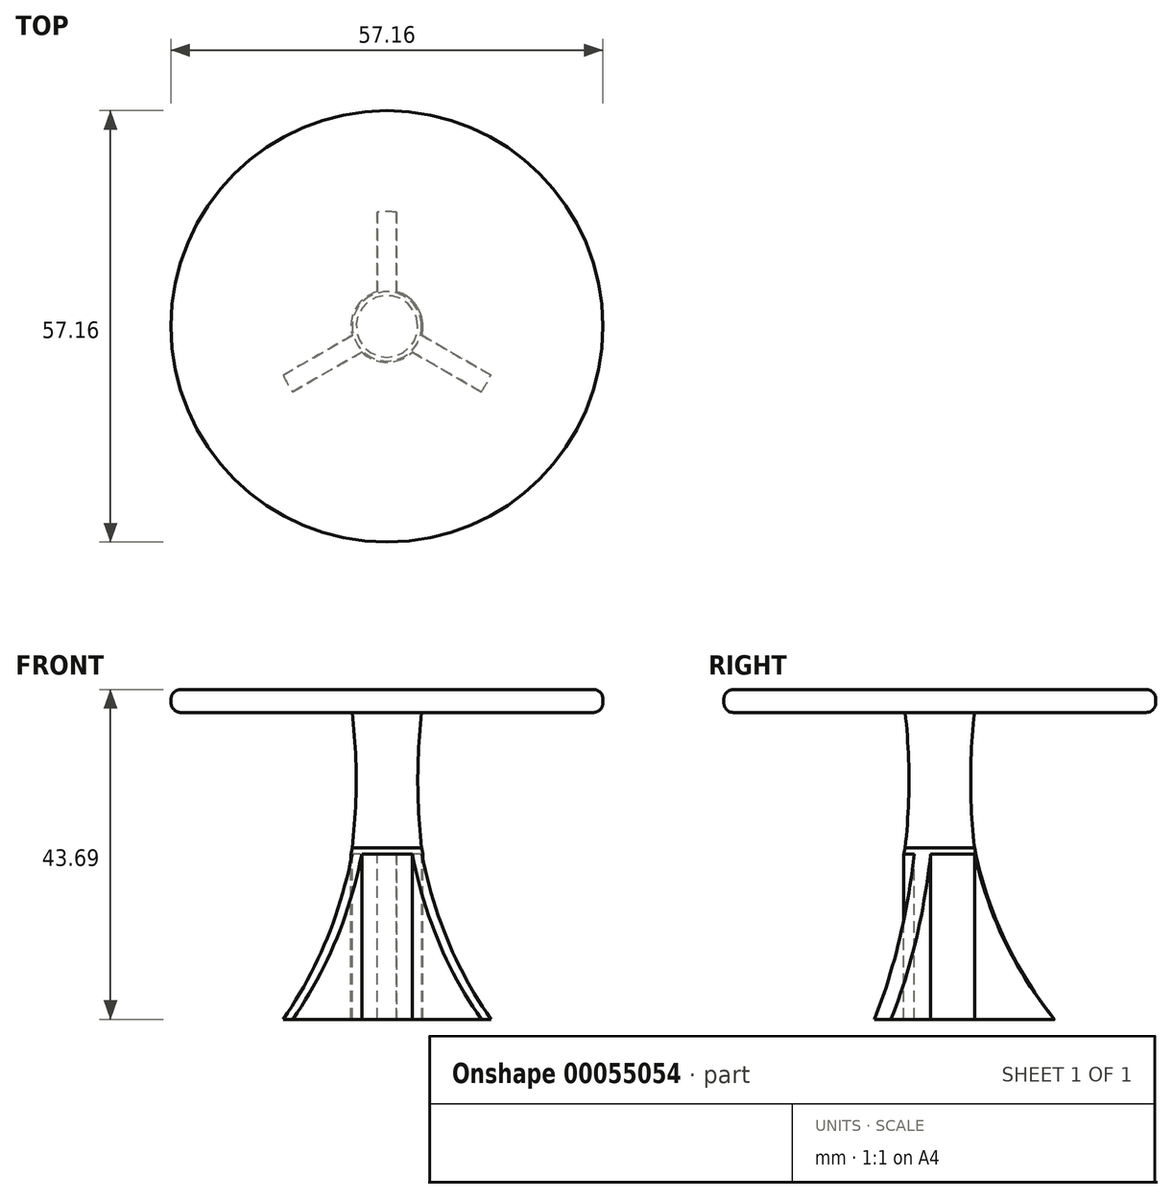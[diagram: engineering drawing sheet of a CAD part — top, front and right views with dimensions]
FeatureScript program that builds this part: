
annotation { "Feature Type Name" : "Feature", "Feature Type Description" : "" }
export const myFeature = defineFeature(function(context is Context, id is Id, definition is map)
    precondition{}
    {
        {
            var Q0;
            Q0=qCreatedBy(makeId("Top.planeOp"),FACE);
            var sketch = newSketch(context, id + "F0", { "sketchPlane" : qUnion([Q0])});
            skCircle(sketch, "E0", {"center": v(0, 0) * mm, "radius": 15.24 * mm});
            skSolve(sketch);
        }
        {
            var Q0;
            Q0 = qSketchRegion(id + "F0", true);
            extrude(context, id + "F1", {"entities" : qUnion([Q0]), "oppositeDirection" : true, "depth" : 40.64 * mm});
        }
        {
            var Q0;
            Q0=qCreatedBy(makeId("Top.planeOp"),FACE);
            var sketch = newSketch(context, id + "F2", { "sketchPlane" : qUnion([Q0])});
            skArc(sketch, "E1", {"start": v(-3.34, -3.4) * mm, "mid": v(0, -4.76) * mm, "end": v(3.34, -3.4) * mm});
            skLineSegment(sketch, "E2", {"start": v(0, 4.76) * mm, "end": v(0, 15.24) * mm, "construction": true});
            skLineSegment(sketch, "E3", {"start": v(-4.12, -2.38) * mm, "end": v(-13.2, -7.62) * mm, "construction": true});
            skLineSegment(sketch, "E4", {"start": v(4.12, -2.38) * mm, "end": v(13.2, -7.62) * mm, "construction": true});
            skLineSegment(sketch, "E5", {"start": v(0, 4.76) * mm, "end": v(-4.12, -2.38) * mm, "construction": true});
            skLineSegment(sketch, "E6", {"start": v(4.12, -2.38) * mm, "end": v(0, 4.76) * mm, "construction": true});
            skLineSegment(sketch, "E7", {"start": v(-4.12, -2.38) * mm, "end": v(4.12, -2.38) * mm, "construction": true});
            skLineSegment(sketch, "E8", {"start": v(-3.34, -3.4) * mm, "end": v(-12.56, -8.72) * mm});
            skLineSegment(sketch, "E9", {"start": v(-13.83, -6.52) * mm, "end": v(-4.61, -1.2) * mm});
            skLineSegment(sketch, "E10", {"start": v(-13.83, -6.52) * mm, "end": v(-13.2, -7.62) * mm, "construction": true});
            skLineSegment(sketch, "E11", {"start": v(-12.56, -8.72) * mm, "end": v(-13.2, -7.62) * mm, "construction": true});
            skLineSegment(sketch, "E12", {"start": v(3.34, -3.4) * mm, "end": v(12.56, -8.72) * mm});
            skLineSegment(sketch, "E13", {"start": v(12.56, -8.72) * mm, "end": v(13.2, -7.62) * mm, "construction": true});
            skLineSegment(sketch, "E14", {"start": v(13.2, -7.62) * mm, "end": v(13.83, -6.52) * mm, "construction": true});
            skLineSegment(sketch, "E15", {"start": v(13.83, -6.52) * mm, "end": v(4.61, -1.2) * mm});
            skLineSegment(sketch, "E16", {"start": v(-1.27, 4.6) * mm, "end": v(-1.27, 15.24) * mm});
            skLineSegment(sketch, "E17", {"start": v(-1.27, 15.24) * mm, "end": v(0, 15.24) * mm, "construction": true});
            skLineSegment(sketch, "E18", {"start": v(0, 15.24) * mm, "end": v(1.27, 15.24) * mm, "construction": true});
            skLineSegment(sketch, "E19", {"start": v(1.27, 15.24) * mm, "end": v(1.27, 4.6) * mm});
            skArc(sketch, "E20.trimOffspring", {"start": v(-1.27, 4.6) * mm, "mid": v(-4.12, 2.38) * mm, "end": v(-4.61, -1.2) * mm});
            skArc(sketch, "E21.trimOffspring", {"start": v(4.61, -1.2) * mm, "mid": v(4.12, 2.38) * mm, "end": v(1.27, 4.6) * mm});
            skArc(sketch, "E22", {"start": v(-1.27, 15.24) * mm, "mid": v(-13.24, 7.65) * mm, "end": v(-13.83, -6.52) * mm});
            skArc(sketch, "E23", {"start": v(13.83, -6.52) * mm, "mid": v(13.24, 7.65) * mm, "end": v(1.27, 15.24) * mm});
            skArc(sketch, "E24", {"start": v(-12.56, -8.72) * mm, "mid": v(0, -15.74) * mm, "end": v(12.56, -8.72) * mm});
            skSolve(sketch);
        }
        {
            var Q0;
            Q0 = qSketchRegion(id + "F2", true);
            extrude(context, id + "F3", {"entities" : qUnion([Q0]), "operationType" : NewBodyOperationType.REMOVE, "endBound" : BoundingType.THROUGH_ALL, "oppositeDirection" : true, "depth" : 25.4 * mm});
        }
        {
            var Q0;
            Q0=qCreatedBy(makeId("Right.planeOp"),FACE);
            var sketch = newSketch(context, id + "F4", { "sketchPlane" : qUnion([Q0])});
            skLineSegment(sketch, "E25", {"start": v(4.6, 0) * mm, "end": v(4.6, -17.91) * mm, "construction": true});
            skLineSegment(sketch, "E26", {"start": v(4.6, -17.91) * mm, "end": v(15.19, -40.64) * mm, "construction": true});
            skArc(sketch, "E27", {"start": v(4.6, 0) * mm, "mid": v(4.08, -8.96) * mm, "end": v(4.6, -17.91) * mm});
            skArc(sketch, "E28", {"start": v(4.6, -17.91) * mm, "mid": v(8.52, -29.92) * mm, "end": v(15.19, -40.64) * mm});
            skLineSegment(sketch, "E29", {"start": v(4.6, 0) * mm, "end": v(18.64, 0) * mm});
            skLineSegment(sketch, "E30", {"start": v(18.64, 0) * mm, "end": v(18.64, -40.63) * mm});
            skLineSegment(sketch, "E31", {"start": v(18.64, -40.63) * mm, "end": v(15.19, -40.64) * mm});
            skLineSegment(sketch, "E32", {"start": v(0, 0) * mm, "end": v(0, 11.15) * mm, "construction": true});
            skSolve(sketch);
        }
        {
            var Q0;
            Q0 = qSketchRegion(id + "F4", true);
            var Q1;
            Q1=sQuery(id+"F4.wireOp",EDGE,"E32");
            revolve(context, id + "F5", {"operationType" : NewBodyOperationType.REMOVE, "entities" : qUnion([Q0]), "axis" : qUnion([Q1]), "revolveType" : RevolveType.FULL, "oppositeDirection" : true});
        }
        {
            var Q0;
            Q0=qCreatedBy(makeId("Top.planeOp"),FACE);
            var sketch = newSketch(context, id + "F6", { "sketchPlane" : qUnion([Q0])});
            skCircle(sketch, "E33", {"center": v(0, 0) * mm, "radius": 28.58 * mm});
            skSolve(sketch);
        }
        {
            var Q0;
            Q0 = qSketchRegion(id + "F6", true);
            extrude(context, id + "F7", {"entities" : qUnion([Q0]), "operationType" : NewBodyOperationType.ADD, "depth" : 3.05 * mm});
        }
        {
            var Q0;
            Q0=makeQuery(id+"F7.opExtrude","CAP_EDGE",EDGE,{"disambiguationData":[OSD([sQuery(id+"F6.wireOp",EDGE,"E33")])],"isStart":false});
            var Q1;
            Q1=makeQuery(id+"F7.opExtrude","CAP_EDGE",EDGE,{"disambiguationData":[OSD([sQuery(id+"F6.wireOp",EDGE,"E33")])],"isStart":true});
            fillet(context, id + "F8", {"entities" : qUnion([Q0, Q1]), "radius" : 1.27 * mm, "tangentPropagation" : true, "allowEdgeOverflow" : false});
        }
    });
